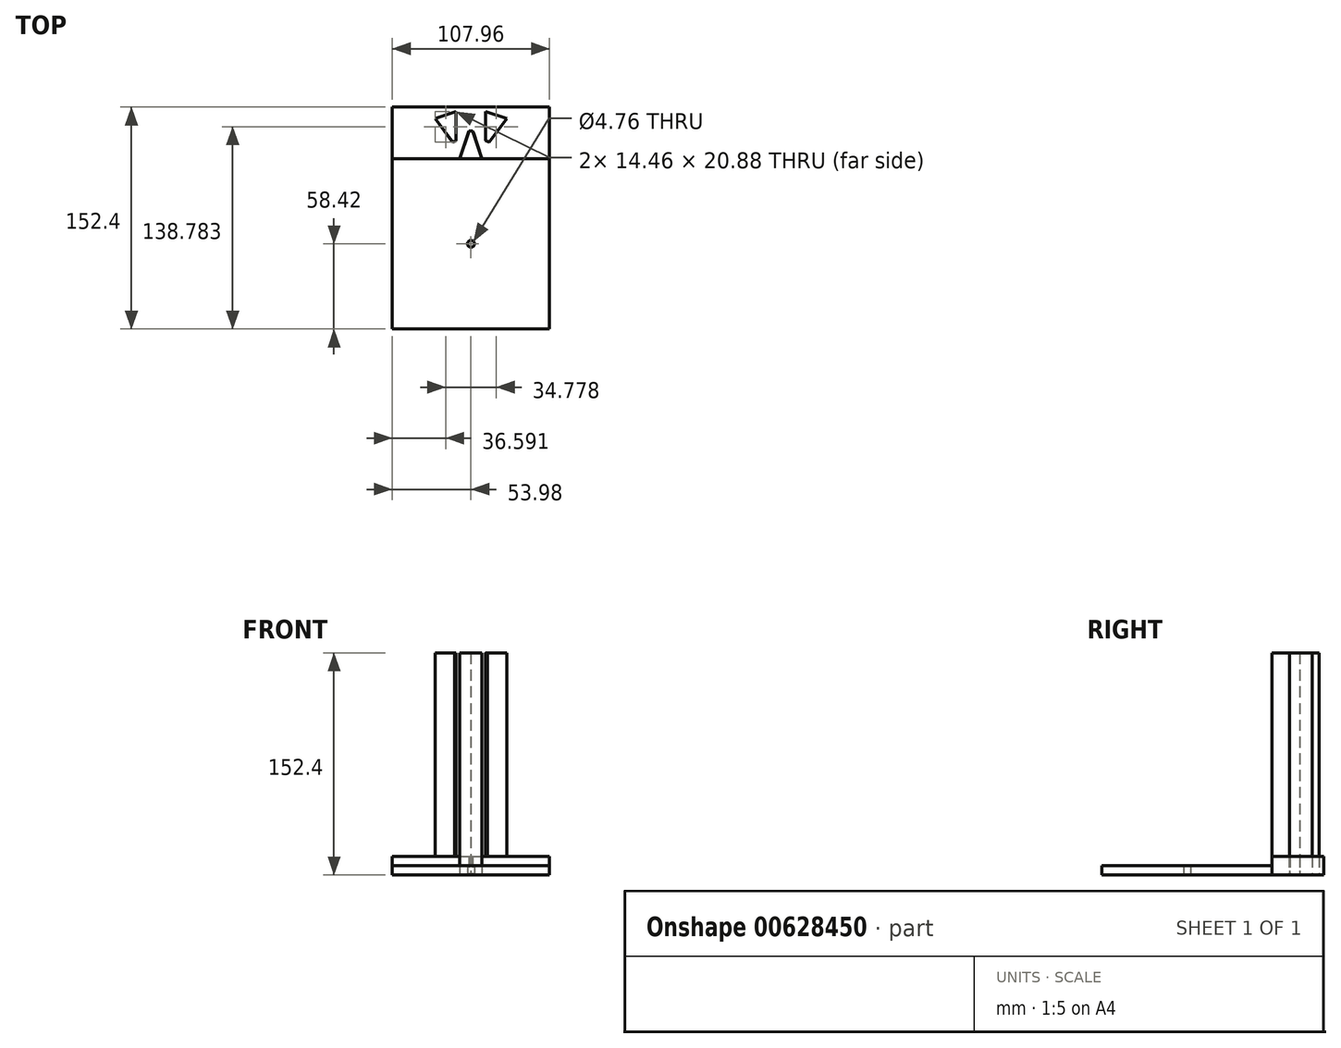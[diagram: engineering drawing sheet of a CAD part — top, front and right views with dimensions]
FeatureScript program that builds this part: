
annotation { "Feature Type Name" : "Feature", "Feature Type Description" : "" }
export const myFeature = defineFeature(function(context is Context, id is Id, definition is map)
    precondition{}
    {
        {
            var Q0;
            Q0=qCreatedBy(makeId("Top.planeOp"),FACE);
            var sketch = newSketch(context, id + "F0", { "sketchPlane" : qUnion([Q0])});
            skLineSegment(sketch, "E0.bottom", {"start": v(-53.97, 58.42) * mm, "end": v(53.98, 58.42) * mm});
            skLineSegment(sketch, "E0.top", {"start": v(-53.98, -58.42) * mm, "end": v(53.97, -58.42) * mm});
            skLineSegment(sketch, "E0.left", {"start": v(-53.97, 58.42) * mm, "end": v(-53.98, -58.42) * mm});
            skLineSegment(sketch, "E0.right", {"start": v(53.98, 58.42) * mm, "end": v(53.97, -58.42) * mm});
            skPoint(sketch, "E0.middle", {"position": v(0, 0) * mm});
            skLineSegment(sketch, "E1.0", {"start": v(-53.98, 93.98) * mm, "end": v(53.97, 93.98) * mm});
            skLineSegment(sketch, "E2", {"start": v(53.97, 93.98) * mm, "end": v(53.98, 58.42) * mm});
            skLineSegment(sketch, "E3", {"start": v(-53.98, 93.98) * mm, "end": v(-53.98, 58.42) * mm});
            skCircle(sketch, "E4", {"center": v(0, 0) * mm, "radius": 2.38 * mm});
            skLineSegment(sketch, "E5", {"start": v(0, 58.42) * mm, "end": v(0, 93.98) * mm});
            skLineSegment(sketch, "E6.0", {"start": v(-53.98, 90.8) * mm, "end": v(53.97, 90.8) * mm});
            skLineSegment(sketch, "E7", {"start": v(-10.16, 90.8) * mm, "end": v(-10.16, 70.65) * mm});
            skLineSegment(sketch, "E8", {"start": v(-24.62, 85.99) * mm, "end": v(-10.16, 90.8) * mm});
            skLineSegment(sketch, "E9", {"start": v(10.16, 90.8) * mm, "end": v(10.16, 70.72) * mm});
            skLineSegment(sketch, "E10", {"start": v(24.62, 85.99) * mm, "end": v(10.16, 90.8) * mm});
            skLineSegment(sketch, "E11", {"start": v(-7.62, 58.42) * mm, "end": v(-1.27, 77.47) * mm});
            skLineSegment(sketch, "E12", {"start": v(7.62, 58.42) * mm, "end": v(-7.62, 58.42) * mm});
            skLineSegment(sketch, "E13", {"start": v(-10.16, 70.72) * mm, "end": v(-12.57, 69.92) * mm});
            skLineSegment(sketch, "E14", {"start": v(-1.27, 77.47) * mm, "end": v(1.27, 77.47) * mm});
            skLineSegment(sketch, "E15", {"start": v(10.16, 70.72) * mm, "end": v(12.57, 69.92) * mm});
            skLineSegment(sketch, "E16", {"start": v(-12.57, 69.92) * mm, "end": v(-12.57, 69.92) * mm});
            skLineSegment(sketch, "E17", {"start": v(1.27, 77.47) * mm, "end": v(7.62, 58.42) * mm});
            skLineSegment(sketch, "E18", {"start": v(10.16, 70.72) * mm, "end": v(10.16, 70.72) * mm});
            skLineSegment(sketch, "E19", {"start": v(12.57, 69.92) * mm, "end": v(24.62, 85.99) * mm});
            skLineSegment(sketch, "E20", {"start": v(-24.62, 85.99) * mm, "end": v(-12.57, 69.92) * mm});
            skSolve(sketch);
        }
        {
            var Q0;
            {var subQ0=sQuery(id+"F0.wireOp",EDGE,"E8");Q0=makeQuery(id+"F0.imprint","IMPRINT",FACE,{"disambiguationData":[TD([[makeQuery(id+"F0.imprint","IMPRINT",EDGE,{"derivedFrom":subQ0}),-1.0]])]});}
            var Q1;
            Q1=makeQuery(id+"F0.imprint","IMPRINT",FACE,{"disambiguationData":[TD([[makeQuery(id+"F0.imprint","IMPRINT",EDGE,{"derivedFrom":sQuery(id+"F0.wireOp",EDGE,"E9")}),1.0]])]});
            var Q2;
            {var subQ5=sQuery(id+"F0.wireOp",EDGE,"E17");Q2=makeQuery(id+"F0.imprint","IMPRINT",FACE,{"disambiguationData":[TD([[makeQuery(id+"F0.imprint","IMPRINT",EDGE,{"derivedFrom":subQ5}),-1.0]])]});}
            var Q3;
            {var subQ5=sQuery(id+"F0.wireOp",EDGE,"E11");Q3=makeQuery(id+"F0.imprint","IMPRINT",FACE,{"disambiguationData":[TD([[makeQuery(id+"F0.imprint","IMPRINT",EDGE,{"derivedFrom":subQ5}),-1.0]])]});}
            extrude(context, id + "F1", {"entities" : qUnion([Q0, Q1, Q2, Q3]), "depth" : 152.4 * mm, "offsetDistance" : 25.4 * mm});
        }
        {
            var Q0;
            Q0=makeQuery(id+"F0.imprint","IMPRINT",FACE,{"disambiguationData":[TD([[makeQuery(id+"F0.imprint","IMPRINT",EDGE,{"derivedFrom":sQuery(id+"F0.wireOp",EDGE,"E0.top")}),1.0]])]});
            extrude(context, id + "F2", {"entities" : qUnion([Q0]), "depth" : 6.35 * mm, "offsetDistance" : 25.4 * mm});
        }
        {
            var Q0;
            {var subQ4=sQuery(id+"F0.wireOp",EDGE,"E8");Q0=makeQuery(id+"F0.imprint","IMPRINT",FACE,{"disambiguationData":[TD([[makeQuery(id+"F0.imprint","IMPRINT",EDGE,{"derivedFrom":subQ4}),1.0]])]});}
            var Q1;
            {var subQ1=sQuery(id+"F0.wireOp",EDGE,"E9");Q1=makeQuery(id+"F0.imprint","IMPRINT",FACE,{"disambiguationData":[TD([[makeQuery(id+"F0.imprint","IMPRINT",EDGE,{"derivedFrom":subQ1}),-1.0]])]});}
            var Q2;
            {var subQ1=sQuery(id+"F0.wireOp",EDGE,"E1.0");var subQ6=sQuery(id+"F0.wireOp",EDGE,"E2");var subQ7=makeQuery(id+"F0.imprint","INTERSECT",VERTEX,{"derivedFrom":[subQ1,subQ6]});Q2=makeQuery(id+"F0.imprint","IMPRINT",FACE,{"disambiguationData":[TD([[makeQuery(id+"F0.imprint","IMPRINT",EDGE,{"disambiguationData":[TD([[subQ7,1.0]])],"derivedFrom":subQ1}),-1.0]])]});}
            var Q3;
            {var subQ1=sQuery(id+"F0.wireOp",EDGE,"E1.0");var subQ5=sQuery(id+"F0.wireOp",EDGE,"E3");var subQ6=makeQuery(id+"F0.imprint","INTERSECT",VERTEX,{"derivedFrom":[subQ1,subQ5]});Q3=makeQuery(id+"F0.imprint","IMPRINT",FACE,{"disambiguationData":[TD([[makeQuery(id+"F0.imprint","IMPRINT",EDGE,{"disambiguationData":[TD([[subQ6,-1.0]])],"derivedFrom":subQ1}),-1.0]])]});}
            extrude(context, id + "F3", {"entities" : qUnion([Q0, Q1, Q2, Q3]), "depth" : 12.7 * mm, "offsetDistance" : 25.4 * mm});
        }
        {
            var Q0;
            Q0=makeQuery(id+"F1.opExtrude","SWEPT_EDGE",EDGE,{"disambiguationData":[OSD([sQuery(id+"F0.wireOp",EDGE,"E7"),sQuery(id+"F0.wireOp",EDGE,"E13")])]});
            var Q1;
            Q1=makeQuery(id+"F1.opExtrude","SWEPT_EDGE",EDGE,{"disambiguationData":[OSD([sQuery(id+"F0.wireOp",EDGE,"E13"),sQuery(id+"F0.wireOp",EDGE,"E20")])]});
            var Q2;
            Q2=makeQuery(id+"F1.opExtrude","SWEPT_EDGE",EDGE,{"disambiguationData":[OSD([sQuery(id+"F0.wireOp",EDGE,"E11"),sQuery(id+"F0.wireOp",EDGE,"E14")])]});
            var Q3;
            Q3=makeQuery(id+"F1.opExtrude","SWEPT_EDGE",EDGE,{"disambiguationData":[OSD([sQuery(id+"F0.wireOp",EDGE,"E14"),sQuery(id+"F0.wireOp",EDGE,"E17")])]});
            var Q4;
            Q4=makeQuery(id+"F1.opExtrude","SWEPT_EDGE",EDGE,{"disambiguationData":[OSD([sQuery(id+"F0.wireOp",EDGE,"E9"),sQuery(id+"F0.wireOp",EDGE,"E15")])]});
            var Q5;
            Q5=makeQuery(id+"F1.opExtrude","SWEPT_EDGE",EDGE,{"disambiguationData":[OSD([sQuery(id+"F0.wireOp",EDGE,"E15"),sQuery(id+"F0.wireOp",EDGE,"E19")])]});
            fillet(context, id + "F4", {"entities" : qUnion([Q0, Q1, Q2, Q3, Q4, Q5]), "radius" : 1.78 * mm, "tangentPropagation" : true, "allowEdgeOverflow" : false});
        }
    });
